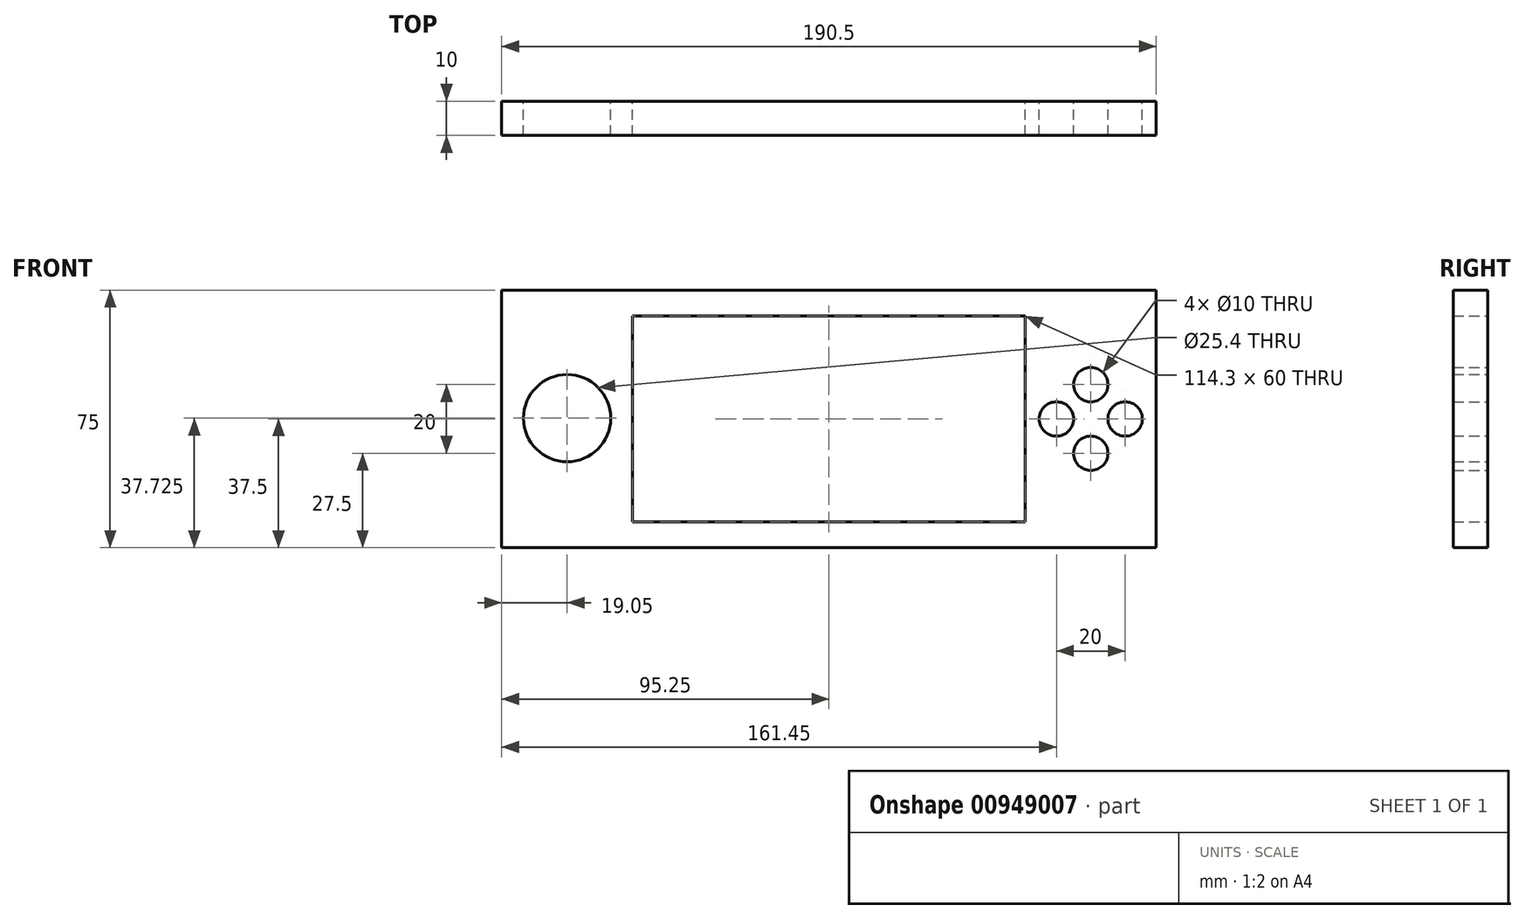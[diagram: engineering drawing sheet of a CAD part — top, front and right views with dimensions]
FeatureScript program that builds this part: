
annotation { "Feature Type Name" : "Feature", "Feature Type Description" : "" }
export const myFeature = defineFeature(function(context is Context, id is Id, definition is map)
    precondition{}
    {
        {
            var Q0;
            Q0=qCreatedBy(makeId("Front.planeOp"),FACE);
            var sketch = newSketch(context, id + "F0", { "sketchPlane" : qUnion([Q0])});
            skLineSegment(sketch, "E0.bottom", {"start": v(0, 0) * mm, "end": v(38.1, 0) * mm});
            skLineSegment(sketch, "E0.top", {"start": v(0, -75) * mm, "end": v(38.1, -75) * mm});
            skLineSegment(sketch, "E0.left", {"start": v(0, 0) * mm, "end": v(0, -75) * mm});
            skLineSegment(sketch, "E0.right", {"start": v(38.1, -7.5) * mm, "end": v(38.1, -67.5) * mm});
            skCircle(sketch, "E1", {"center": v(19.05, -37.27) * mm, "radius": 12.7 * mm});
            skPoint(sketch, "E2.start.orphan", {"position": v(19.05, 0) * mm});
            skLineSegment(sketch, "E3", {"start": v(38.1, -75) * mm, "end": v(152.4, -75) * mm});
            skLineSegment(sketch, "E4", {"start": v(38.1, 0) * mm, "end": v(152.4, 0) * mm});
            skLineSegment(sketch, "E5.bottom", {"start": v(152.4, -75) * mm, "end": v(190.5, -75) * mm});
            skLineSegment(sketch, "E5.top", {"start": v(152.4, 0) * mm, "end": v(190.5, 0) * mm});
            skLineSegment(sketch, "E5.left", {"start": v(152.4, -67.5) * mm, "end": v(152.4, -7.5) * mm});
            skLineSegment(sketch, "E5.right", {"start": v(190.5, -75) * mm, "end": v(190.5, 0) * mm});
            skCircle(sketch, "E6", {"center": v(161.45, -37.5) * mm, "radius": 5 * mm});
            skCircle(sketch, "E7", {"center": v(171.45, -47.5) * mm, "radius": 5 * mm});
            skCircle(sketch, "E8", {"center": v(181.45, -37.5) * mm, "radius": 5 * mm});
            skCircle(sketch, "E9", {"center": v(171.45, -27.5) * mm, "radius": 5 * mm});
            skPoint(sketch, "E10.orphan", {"position": v(171.45, 0) * mm});
            skPoint(sketch, "E11.orphan", {"position": v(171.45, -37.5) * mm});
            skLineSegment(sketch, "E12", {"start": v(89.19, -67.5) * mm, "end": v(38.1, -67.5) * mm});
            skLineSegment(sketch, "E13", {"start": v(91.58, -7.5) * mm, "end": v(38.1, -7.5) * mm});
            skLineSegment(sketch, "E14", {"start": v(91.58, -7.5) * mm, "end": v(152.4, -7.5) * mm});
            skLineSegment(sketch, "E15", {"start": v(89.19, -67.5) * mm, "end": v(152.4, -67.5) * mm});
            skPoint(sketch, "E16.orphan", {"position": v(45.6, 0) * mm});
            skPoint(sketch, "E17.orphan", {"position": v(144.9, 0) * mm});
            skSolve(sketch);
        }
        {
            var Q0;
            Q0 = qSketchRegion(id + "F0", true);
            extrude(context, id + "F1", {"entities" : qUnion([Q0]), "depth" : 10 * mm, "offsetDistance" : 25 * mm});
        }
    });
